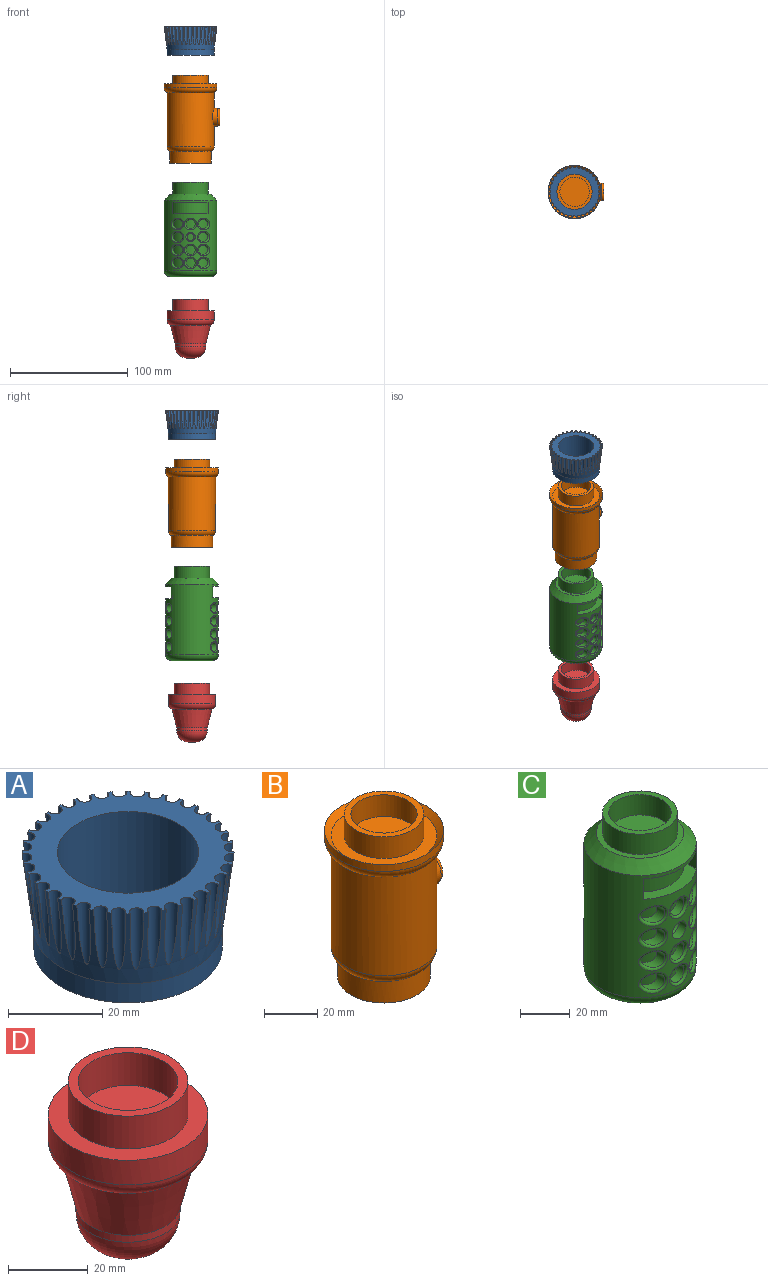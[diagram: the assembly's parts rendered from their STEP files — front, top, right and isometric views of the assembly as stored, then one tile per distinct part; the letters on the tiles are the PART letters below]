
ASSEMBLY  parts=4 mates=2
PART A: 41 faces, bbox 45x45x25 mm
  f0: plane 44.92x44.92mm, normal (0,0,1), area 704.9mm2, adj f3,f4,f5,f6,f7,f8,f9,f10
  f1: cylinder r=20mm len=40mm, axis (0,0,-1), area 628.3mm2, adj f2,f3
  f2: plane 40x40mm, normal (0,0,-1), area 549.8mm2, adj f1,f4
  f3: cone r=20mm half-angle=7.1deg, axis (0,0,1), area 1684.5mm2, adj f0,f1,f5,f6,f7,f8,f9,f10
  f4: cylinder r=15mm len=30mm, axis (0,0,-1), area 2356.2mm2, adj f0,f2
  f5: cylinder r=1.5mm len=16.01mm, axis (0,0,-1), area 54.9mm2, adj f0,f3
  f6: cylinder r=1.5mm len=16.01mm, axis (0,0,-1), area 54.9mm2, adj f0,f3
  f7: cylinder r=1.5mm len=16.01mm, axis (0,0,-1), area 54.9mm2, adj f0,f3
  f8: cylinder r=1.5mm len=16.01mm, axis (0,0,-1), area 54.9mm2, adj f0,f3
  f9: cylinder r=1.5mm len=16.01mm, axis (0,0,-1), area 54.9mm2, adj f0,f3
  f10: cylinder r=1.5mm len=16.01mm, axis (0,0,-1), area 54.9mm2, adj f0,f3
  f11: cylinder r=1.5mm len=16.01mm, axis (0,0,-1), area 54.9mm2, adj f0,f3
  f12: cylinder r=1.5mm len=16.01mm, axis (0,0,-1), area 54.9mm2, adj f0,f3
  f13: cylinder r=1.5mm len=16.01mm, axis (0,0,-1), area 54.9mm2, adj f0,f3
  f14: cylinder r=1.5mm len=16.01mm, axis (0,0,-1), area 54.9mm2, adj f0,f3
  f15: cylinder r=1.5mm len=16.01mm, axis (0,0,-1), area 54.9mm2, adj f0,f3
  f16: cylinder r=1.5mm len=16.01mm, axis (0,0,-1), area 54.9mm2, adj f0,f3
  f17: cylinder r=1.5mm len=16.01mm, axis (0,0,-1), area 54.9mm2, adj f0,f3
  f18: cylinder r=1.5mm len=16.01mm, axis (0,0,-1), area 55.5mm2, adj f0,f3
  f19: cylinder r=1.5mm len=16.01mm, axis (0,0,-1), area 54.9mm2, adj f0,f3
  f20: cylinder r=1.5mm len=16.01mm, axis (0,0,-1), area 54.9mm2, adj f0,f3
  f21: cylinder r=1.5mm len=16.01mm, axis (0,0,-1), area 54.9mm2, adj f0,f3
  f22: cylinder r=1.5mm len=16.01mm, axis (0,0,-1), area 54.9mm2, adj f0,f3
  f23: cylinder r=1.5mm len=16.01mm, axis (0,0,-1), area 54.9mm2, adj f0,f3
  f24: cylinder r=1.5mm len=16.01mm, axis (0,0,-1), area 54.9mm2, adj f0,f3
  f25: cylinder r=1.5mm len=16.01mm, axis (0,0,-1), area 54.9mm2, adj f0,f3
  f26: cylinder r=1.5mm len=16.01mm, axis (0,0,-1), area 54.9mm2, adj f0,f3
  f27: cylinder r=1.5mm len=16.01mm, axis (0,0,-1), area 54.9mm2, adj f0,f3
  f28: cylinder r=1.5mm len=16.01mm, axis (0,0,-1), area 54.9mm2, adj f0,f3
  f29: cylinder r=1.5mm len=16.01mm, axis (0,0,-1), area 54.9mm2, adj f0,f3
  f30: cylinder r=1.5mm len=16.01mm, axis (0,0,-1), area 54.9mm2, adj f0,f3
  f31: cylinder r=1.5mm len=16.01mm, axis (0,0,-1), area 54.9mm2, adj f0,f3
  f32: cylinder r=1.5mm len=16.01mm, axis (0,0,-1), area 54.9mm2, adj f0,f3
  f33: cylinder r=1.5mm len=16.01mm, axis (0,0,-1), area 54.9mm2, adj f0,f3
  f34: cylinder r=1.5mm len=16.01mm, axis (0,0,-1), area 54.9mm2, adj f0,f3
  f35: cylinder r=1.5mm len=16.01mm, axis (0,0,-1), area 54.9mm2, adj f0,f3
  f36: cylinder r=1.5mm len=16.01mm, axis (0,0,-1), area 54.9mm2, adj f0,f3
  f37: cylinder r=1.5mm len=16.01mm, axis (0,0,-1), area 54.9mm2, adj f0,f3
  f38: cylinder r=1.5mm len=16.01mm, axis (0,0,-1), area 54.9mm2, adj f0,f3
  f39: cylinder r=1.5mm len=16.01mm, axis (0,0,-1), area 54.9mm2, adj f0,f3
  f40: cylinder r=1.5mm len=16.01mm, axis (0,0,-1), area 54.9mm2, adj f0,f3
PART B: 17 faces, bbox 49.4x48.7x75 mm
  f0: plane 11x11mm, normal (1,0,0), area 95mm2, adj f10
  f1: cylinder r=7.5mm len=15mm, axis (1,0,0), area 175.4mm2, adj f2,f10
  f2: cylinder r=20mm len=45.67mm, axis (0,0,-1), area 5558.7mm2, adj f1,f5,f8
  f3: cylinder r=17.5mm len=35mm, axis (0,0,-1), area 1099.6mm2, adj f4,f5
  f4: plane 35x35mm, normal (0,0,-1), area 255.3mm2, adj f3,f11
  f5: torus R=15mm, axis (0,0,-1), area 629.5mm2, adj f2,f3
  f6: cylinder r=22.5mm len=45mm, axis (0,0,-1), area 448.1mm2, adj f7,f8
  f7: cone r=20mm half-angle=45deg, axis (0,0,1), area 472.1mm2, adj f6,f9
  f8: torus R=17.5mm, axis (0,0,-1), area 711.8mm2, adj f2,f6
  f9: plane 40x40mm, normal (0,0,1), area 549.8mm2, adj f7,f14
  f10: torus R=5.5mm, axis (1,0,0), area 133.7mm2, adj f0,f1
  f11: cylinder r=15mm len=60mm, axis (0,0,-1), area 5654.9mm2, adj f4,f12
  f12: plane 30x30mm, normal (0,0,-1), area 706.9mm2, adj f11
  f13: cylinder r=12.5mm len=25mm, axis (0,0,-1), area 785.4mm2, adj f15,f16
  f14: cylinder r=15mm len=30mm, axis (0,0,-1), area 942.5mm2, adj f9,f15
  f15: plane 30x30mm, normal (0,0,1), area 216mm2, adj f13,f14
  f16: plane 25x25mm, normal (0,0,1), area 490.9mm2, adj f13
PART C: 81 faces, bbox 48.7x48.7x80 mm
  f0: cylinder r=17.5mm len=8mm, axis (0,0,-1), area 65.4mm2, adj f2
  f1: cylinder r=22.5mm len=60mm, axis (0,0,-1), area 6090.8mm2, adj f3,f5,f7,f9,f11,f13,f15,f17
  f2: cylinder r=4mm len=11.17mm, axis (0,-1,0), area 121.2mm2, adj f0,f79
  f3: cylinder r=4mm len=11.92mm, axis (0,-1,0), area 154.8mm2, adj f1,f60
  f4: cylinder r=4mm len=11.17mm, axis (0,-1,0), area 121.2mm2, adj f59,f78
  f5: cylinder r=4mm len=11.92mm, axis (0,-1,0), area 154.8mm2, adj f1,f58
  f6: cylinder r=4mm len=11.17mm, axis (0,-1,0), area 121.2mm2, adj f57,f77
  f7: cylinder r=4mm len=11.92mm, axis (0,-1,0), area 154.8mm2, adj f1,f56
  f8: cylinder r=4mm len=8mm, axis (0,-1,0), area 99mm2, adj f55,f76
  f9: cylinder r=4mm len=8mm, axis (0,-1,0), area 127mm2, adj f1,f54
  f10: cylinder r=4mm len=8mm, axis (0,-1,0), area 99mm2, adj f53,f75
  f11: cylinder r=4mm len=8mm, axis (0,-1,0), area 127mm2, adj f1,f52
  f12: cylinder r=4mm len=11.17mm, axis (0,-1,0), area 121.2mm2, adj f51,f74
  f13: cylinder r=4mm len=11.92mm, axis (0,-1,0), area 154.8mm2, adj f1,f50
  f14: cylinder r=4mm len=11.17mm, axis (0,-1,0), area 121.2mm2, adj f49,f73
  f15: cylinder r=4mm len=11.92mm, axis (0,-1,0), area 154.8mm2, adj f1,f48
  f16: cylinder r=4mm len=8mm, axis (0,-1,0), area 99mm2, adj f47,f72
  f17: cylinder r=4mm len=8mm, axis (0,-1,0), area 127mm2, adj f1,f46
  f18: cylinder r=4mm len=8mm, axis (0,-1,0), area 99.1mm2, adj f1,f71
  f19: cylinder r=4mm len=8mm, axis (0,-1,0), area 127mm2, adj f1,f44
  f20: cylinder r=4mm len=11.17mm, axis (0,-1,0), area 121.2mm2, adj f43,f70
  f21: cylinder r=4mm len=11.92mm, axis (0,-1,0), area 154.8mm2, adj f1,f42
  f22: cylinder r=4mm len=11.17mm, axis (0,-1,0), area 121.2mm2, adj f41,f69
  f23: cylinder r=4mm len=11.92mm, axis (0,-1,0), area 154.8mm2, adj f1,f40
  f24: cylinder r=4mm len=11.17mm, axis (0,-1,0), area 121.2mm2, adj f39,f68
  f25: cylinder r=4mm len=11.92mm, axis (0,-1,0), area 154.8mm2, adj f1,f38
  f26: plane 10x7.76mm, normal (-1,0,0), area 77.6mm2, adj f1,f27,f29,f37
  f27: plane 30x13.49mm, normal (0,0,-1), area 170.4mm2, adj f1,f26,f28,f37
  f28: plane 10x7.76mm, normal (1,0,0), area 77.6mm2, adj f1,f27,f29,f37
  f29: plane 30x13.49mm, normal (0,0,1), area 170.4mm2, adj f1,f26,f28,f37
  f30: plane 10x7.76mm, normal (1,0,0), area 77.6mm2, adj f1,f31,f32,f36
  f31: plane 30x13.49mm, normal (0,0,1), area 170.4mm2, adj f1,f30,f33,f36
  f32: plane 30x13.49mm, normal (0,0,-1), area 170.4mm2, adj f1,f30,f33,f36
  f33: plane 10x7.76mm, normal (-1,0,0), area 77.6mm2, adj f1,f31,f32,f36
  f34: plane 35x35mm, normal (0,0,-1), area 255.3mm2, adj f65,f80
  f35: plane 35x35mm, normal (0,0,1), area 255.3mm2, adj f62,f67
  f36: cylinder r=17.5mm len=30mm, axis (0,0,-1), area 360.4mm2, adj f30,f31,f32,f33
  f37: cylinder r=17.5mm len=30mm, axis (0,0,-1), area 360.4mm2, adj f26,f27,f28,f29
  f38: cylinder r=17.5mm len=8mm, axis (0,0,-1), area 65.4mm2, adj f25
  f39: cylinder r=17.5mm len=8mm, axis (0,0,-1), area 65.4mm2, adj f24
  f40: cylinder r=17.5mm len=8mm, axis (0,0,-1), area 65.4mm2, adj f23
  f41: cylinder r=17.5mm len=8mm, axis (0,0,-1), area 65.4mm2, adj f22
  f42: cylinder r=17.5mm len=8mm, axis (0,0,-1), area 65.4mm2, adj f21
  f43: cylinder r=17.5mm len=8mm, axis (0,0,-1), area 65.4mm2, adj f20
  f44: cylinder r=17.5mm len=8mm, axis (0,0,-1), area 50.6mm2, adj f19
  f45: cylinder r=17.5mm len=6mm, axis (0,0,-1), area 26.8mm2, adj f71
  f46: cylinder r=17.5mm len=8mm, axis (0,0,-1), area 50.6mm2, adj f17
  f47: cylinder r=17.5mm len=8mm, axis (0,0,-1), area 50.6mm2, adj f16
  f48: cylinder r=17.5mm len=8mm, axis (0,0,-1), area 65.4mm2, adj f15
  f49: cylinder r=17.5mm len=8mm, axis (0,0,-1), area 65.4mm2, adj f14
  f50: cylinder r=17.5mm len=8mm, axis (0,0,-1), area 65.4mm2, adj f13
  f51: cylinder r=17.5mm len=8mm, axis (0,0,-1), area 65.4mm2, adj f12
  f52: cylinder r=17.5mm len=8mm, axis (0,0,-1), area 50.6mm2, adj f11
  f53: cylinder r=17.5mm len=8mm, axis (0,0,-1), area 50.6mm2, adj f10
  f54: cylinder r=17.5mm len=8mm, axis (0,0,-1), area 50.6mm2, adj f9
  f55: cylinder r=17.5mm len=8mm, axis (0,0,-1), area 50.6mm2, adj f8
  f56: cylinder r=17.5mm len=8mm, axis (0,0,-1), area 65.4mm2, adj f7
  f57: cylinder r=17.5mm len=8mm, axis (0,0,-1), area 65.4mm2, adj f6
  f58: cylinder r=17.5mm len=8mm, axis (0,0,-1), area 65.4mm2, adj f5
  f59: cylinder r=17.5mm len=8mm, axis (0,0,-1), area 65.4mm2, adj f4
  f60: cylinder r=17.5mm len=8mm, axis (0,0,-1), area 65.4mm2, adj f3
  f61: cylinder r=12.5mm len=25mm, axis (0,0,-1), area 785.4mm2, adj f63,f64
  f62: cylinder r=15mm len=30mm, axis (0,0,-1), area 942.5mm2, adj f35,f63
  f63: plane 30x30mm, normal (0,0,1), area 216mm2, adj f61,f62
  f64: plane 25x25mm, normal (0,0,1), area 490.9mm2, adj f61
  f65: cylinder r=15mm len=65mm, axis (0,0,-1), area 6126.1mm2, adj f34,f66
  f66: plane 30x30mm, normal (0,0,-1), area 706.9mm2, adj f65
  f67: cone r=17.5mm half-angle=45deg, axis (0,0,-1), area 888.6mm2, adj f1,f35
  f68: bspline ~10.47x10.02mm, area 52.3mm2, adj f1,f24
  f69: bspline ~10.47x10.02mm, area 52.3mm2, adj f1,f22
  f70: bspline ~10.47x10.02mm, area 52.3mm2, adj f1,f20
  f71: bspline ~8.01x8.01mm, area 37.5mm2, adj f18,f45
  f72: bspline ~10.48x10.01mm, area 46.9mm2, adj f1,f16
  f73: bspline ~10.47x10.02mm, area 52.2mm2, adj f1,f14
  f74: bspline ~10.47x10.02mm, area 52.2mm2, adj f1,f12
  f75: bspline ~10.48x10.01mm, area 46.9mm2, adj f1,f10
  f76: bspline ~10.48x10.01mm, area 46.9mm2, adj f1,f8
  f77: bspline ~10.47x10.02mm, area 52.2mm2, adj f1,f6
  f78: bspline ~10.47x10.02mm, area 52.2mm2, adj f1,f4
  f79: bspline ~10.47x10.02mm, area 52.3mm2, adj f1,f2
  f80: torus R=17.5mm, axis (0,0,1), area 1020.7mm2, adj f1,f34
PART D: 11 faces, bbox 43.3x43.3x50 mm
  f0: cylinder r=13.03mm len=26.05mm, axis (0,0,1), area 172.5mm2, adj f1,f5
  f1: cone r=13.03mm half-angle=14deg, axis (0,0,1), area 1533.3mm2, adj f0,f6
  f2: cylinder r=20mm len=40mm, axis (0,0,1), area 944.3mm2, adj f3,f6
  f3: plane 40x40mm, normal (0,0,1), area 549.8mm2, adj f2,f8
  f4: plane 6.05x6.05mm, normal (0,0,-1), area 28.8mm2, adj f5
  f5: torus R=3.03mm, axis (0,0,1), area 927.1mm2, adj f0,f4
  f6: torus R=15mm, axis (0,0,-1), area 693.4mm2, adj f1,f2
  f7: cylinder r=12.5mm len=25mm, axis (0,0,-1), area 785.4mm2, adj f9,f10
  f8: cylinder r=15mm len=30mm, axis (0,0,-1), area 942.5mm2, adj f3,f9
  f9: plane 30x30mm, normal (0,0,1), area 216mm2, adj f7,f8
  f10: plane 25x25mm, normal (0,0,1), area 490.9mm2, adj f7
PLACE A t=(-24.84,113.88,46.86)mm
PLACE B t=(-24.84,113.88,-44.84)mm
PLACE C t=(-24.84,113.88,-141.24)mm
PLACE D t=(-24.84,113.88,-182.65)mm
MATE slider A.f1 <-> B.f14  axis (0,0,-1) through (-24.84,113.88,46.86)mm
MATE slider B.f11 <-> C.f62  axis (0,0,-1) through (-24.84,113.88,-44.84)mm
